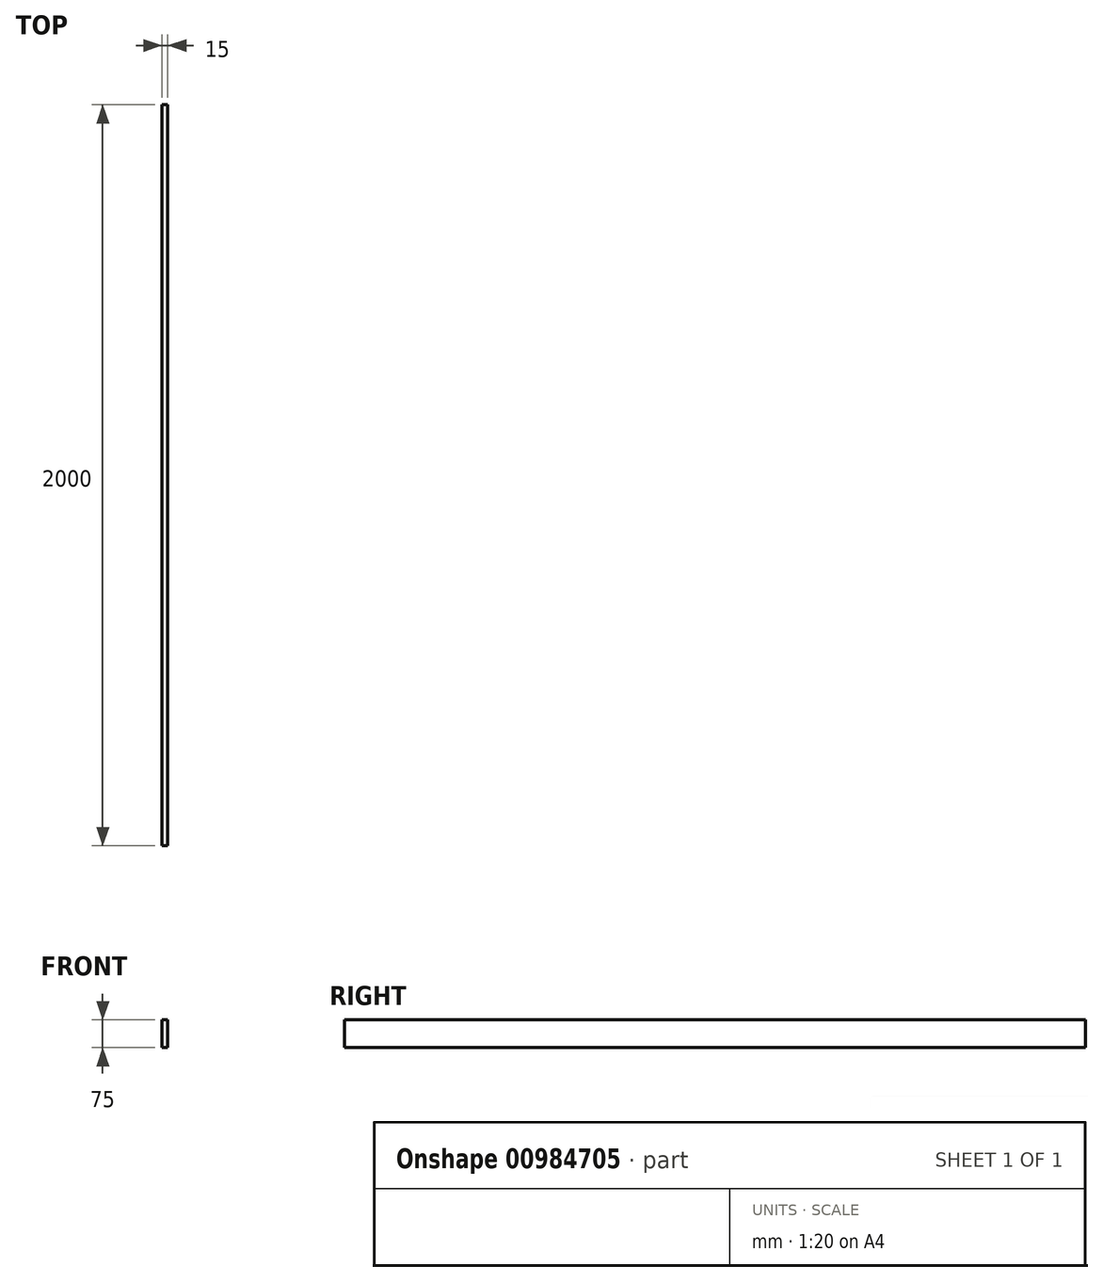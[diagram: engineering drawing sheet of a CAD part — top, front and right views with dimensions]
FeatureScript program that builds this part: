
annotation { "Feature Type Name" : "Feature", "Feature Type Description" : "" }
export const myFeature = defineFeature(function(context is Context, id is Id, definition is map)
    precondition{}
    {
        {
            var Q0;
            Q0=qCreatedBy(makeId("Front.planeOp"),FACE);
            var sketch = newSketch(context, id + "F0", { "sketchPlane" : qUnion([Q0])});
            skLineSegment(sketch, "E0.bottom", {"start": v(0, 0) * mm, "end": v(15, 0) * mm});
            skLineSegment(sketch, "E0.top", {"start": v(0, 75) * mm, "end": v(15, 75) * mm});
            skLineSegment(sketch, "E0.left", {"start": v(0, 0) * mm, "end": v(0, 75) * mm});
            skLineSegment(sketch, "E0.right", {"start": v(15, 0) * mm, "end": v(15, 75) * mm});
            skSolve(sketch);
        }
        {
            var Q0;
            Q0=qSketchRegion(id+"F0",true);
            extrude(context, id + "F1", {"entities" : qUnion([Q0]), "depth" : 2000 * mm, "offsetDistance" : 25 * mm});
        }
    });
